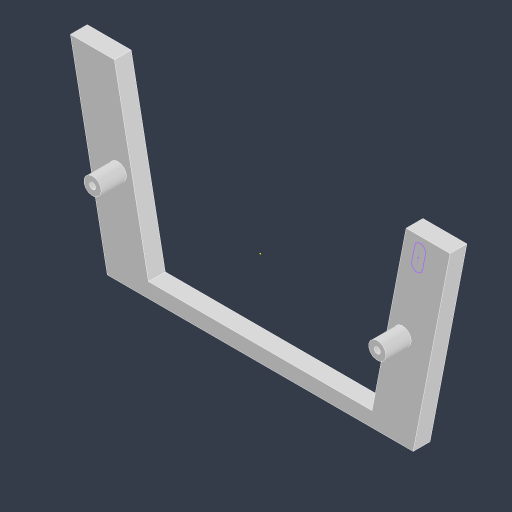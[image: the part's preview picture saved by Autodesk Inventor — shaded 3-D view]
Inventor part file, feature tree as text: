
AUTODESK INVENTOR PART (.ipt)
format: ipt  version: 2023.4 (Build 274418000, 418)  size: 124,416 bytes
history: native  units: mm
features: sketch x4, extrude x3
ambient origin geometry x8: Origin, YZ Plane, XZ Plane, XY Plane, X Axis, Y Axis, Z Axis, Center Point
bodies: Solid1 (feature_tree)
feature tree (7):
  extrude  "Extrusion1"  Depth=45.0mm
  extrude  "Extrusion2"  TaperAngle=0.0deg  [1 undecoded]
  extrude  "Extrusion3"  Depth=4.1mm
  sketch  "Sketch4"  dims[d7=22.5mm d8=45.0mm d9=1.5mm d10=6.0mm d11=0.0mm d13=60.4mm d14=19.0mm d15=0.0mm d16=0.0mm]
  sketch  "Sketch1"  dims[d0=45.0mm d1=3.839724mm]
  sketch  "Sketch2"  dims[d2=90.0mm d4=0.0mm]
  sketch  "Sketch3"  dims[d5=67.5mm d6=4.1mm]
note: 1 required parameter value undecoded (feature->parameter linkage not recoverable at this tier; creation-order binding heuristic only, values carry confidence <= 0.55)
